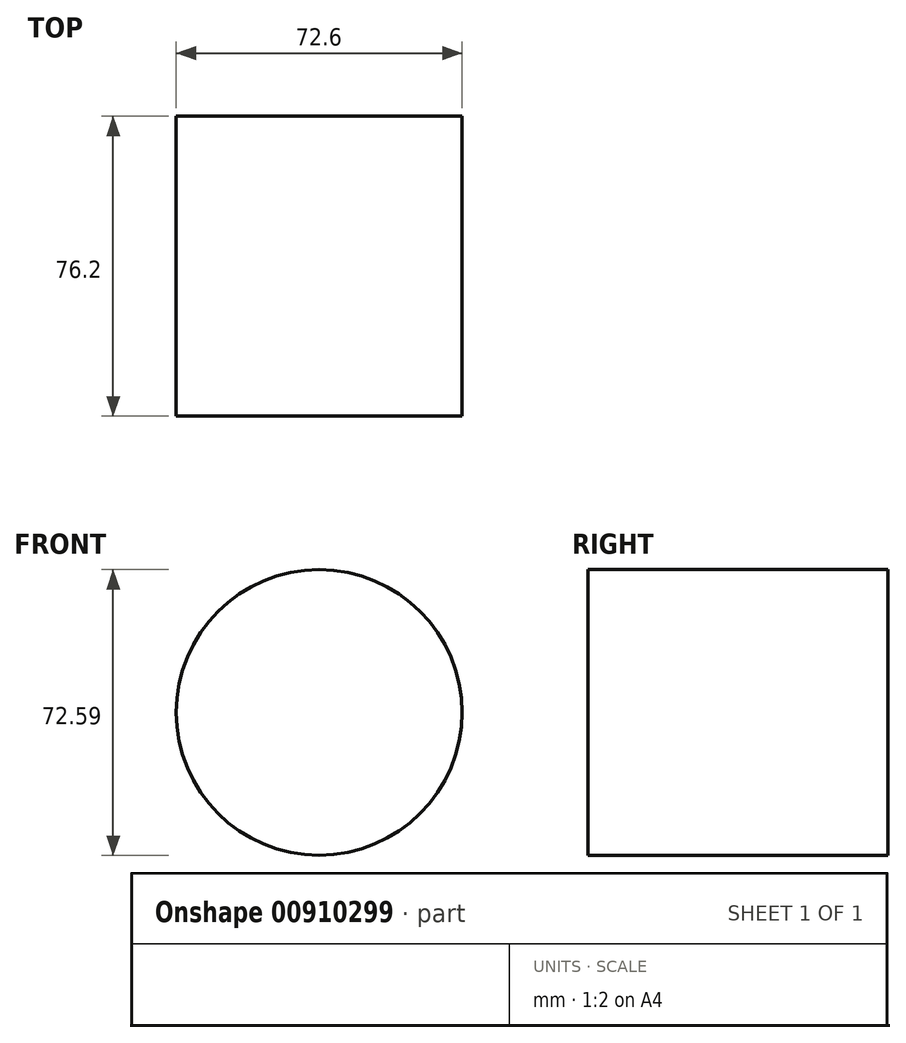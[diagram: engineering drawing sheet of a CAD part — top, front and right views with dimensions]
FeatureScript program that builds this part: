
annotation { "Feature Type Name" : "Feature", "Feature Type Description" : "" }
export const myFeature = defineFeature(function(context is Context, id is Id, definition is map)
    precondition{}
    {
        {
            var Q0;
            Q0=qCreatedBy(makeId("Front.planeOp"),FACE);
            var sketch = newSketch(context, id + "F0", { "sketchPlane" : qUnion([Q0])});
            skCircle(sketch, "E0", {"center": v(22.59, 46.59) * mm, "radius": 36.3 * mm});
            skSolve(sketch);
        }
        {
            var Q0;
            Q0=makeQuery(id+"F0.imprint","IMPRINT",FACE,{"disambiguationData":[TD([[makeQuery(id+"F0.imprint","IMPRINT",EDGE,{"derivedFrom":sQuery(id+"F0.wireOp",EDGE,"E0")}),1.0]])]});
            extrude(context, id + "F1", {"entities" : qUnion([Q0]), "depth" : 76.2 * mm, "offsetDistance" : 25.4 * mm});
        }
    });
